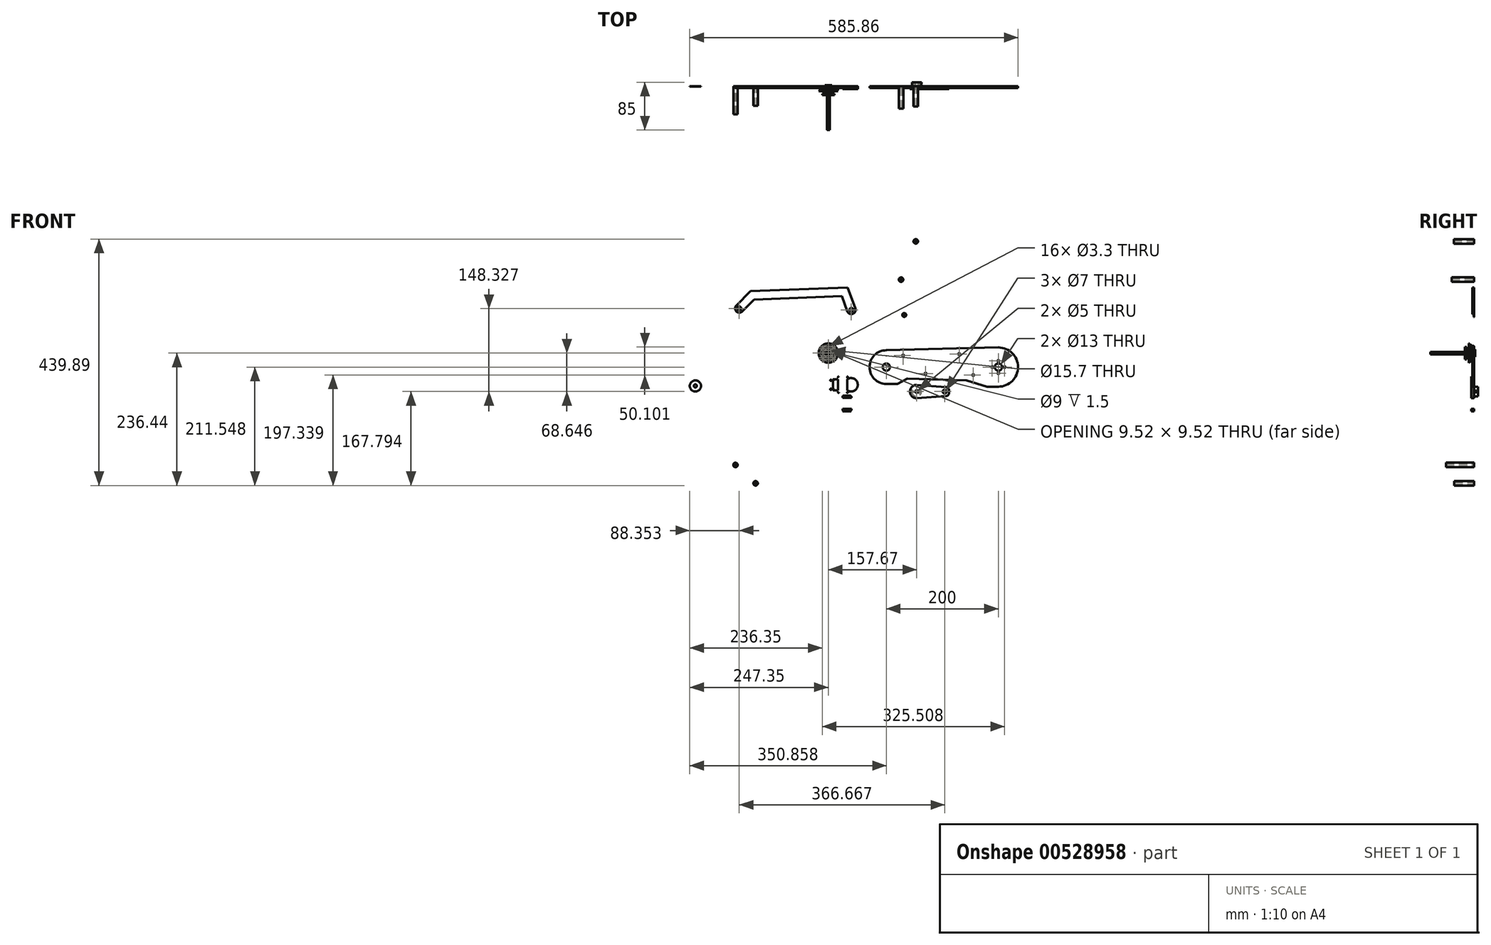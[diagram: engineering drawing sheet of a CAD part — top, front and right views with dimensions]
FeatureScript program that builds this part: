
annotation { "Feature Type Name" : "Feature", "Feature Type Description" : "" }
export const myFeature = defineFeature(function(context is Context, id is Id, definition is map)
    precondition{}
    {
        {
            var Q0;
            Q0=qCreatedBy(makeId("Front.planeOp"),FACE);
            var sketch = newSketch(context, id + "F0", { "sketchPlane" : qUnion([Q0])});
            skCircle(sketch, "E0", {"center": v(103.5, -24.9) * mm, "radius": 6.5 * mm});
            skCircle(sketch, "E1", {"center": v(303.5, -24.9) * mm, "radius": 11 * mm, "construction": true});
            skArc(sketch, "E2", {"start": v(103.5, -54.9) * mm, "mid": v(73.5, -24.9) * mm, "end": v(103.5, 5.1) * mm});
            skLineSegment(sketch, "E3", {"start": v(103.5, -54.9) * mm, "end": v(123.5, -54.9) * mm});
            skArc(sketch, "E4", {"start": v(303.5, -59.9) * mm, "mid": v(338.5, -24.9) * mm, "end": v(303.5, 10.1) * mm});
            skLineSegment(sketch, "E5", {"start": v(303.5, -59.9) * mm, "end": v(283.5, -59.9) * mm});
            skLineSegment(sketch, "E6", {"start": v(103.5, 5.1) * mm, "end": v(303.5, 10.1) * mm});
            skLineSegment(sketch, "E7", {"start": v(123.5, -54.9) * mm, "end": v(283.5, -59.9) * mm, "construction": true});
            skLineSegment(sketch, "E8", {"start": v(123.5, -54.9) * mm, "end": v(141.13, -45.44) * mm});
            skPoint(sketch, "E9", {"position": v(133.5, -4.14) * mm});
            skPoint(sketch, "E10", {"position": v(233.5, -1.64) * mm});
            skLineSegment(sketch, "E11", {"start": v(133.5, -4.14) * mm, "end": v(233.5, -1.64) * mm, "construction": true});
            skPoint(sketch, "E12", {"position": v(173.5, -36.44) * mm});
            skPoint(sketch, "E13", {"position": v(258.5, -39.1) * mm});
            skLineSegment(sketch, "E14", {"start": v(246.52, -48.73) * mm, "end": v(283.5, -59.9) * mm});
            skLineSegment(sketch, "E15", {"start": v(141.13, -45.44) * mm, "end": v(246.52, -48.73) * mm});
            skLineSegment(sketch, "E16", {"start": v(173.5, -36.44) * mm, "end": v(258.5, -39.1) * mm, "construction": true});
            skCircle(sketch, "E17", {"center": v(103.5, 25.51) * mm, "radius": 3.5 * mm});
            skArc(sketch, "E18", {"start": v(98.2, 30.82) * mm, "mid": v(98.2, 20.2) * mm, "end": v(108.81, 20.2) * mm});
            skLineSegment(sketch, "E19", {"start": v(123.68, 56.29) * mm, "end": v(98.2, 30.82) * mm});
            skLineSegment(sketch, "E20", {"start": v(108.81, 20.2) * mm, "end": v(130.12, 41.52) * mm});
            skCircle(sketch, "E21", {"center": v(303.5, 23) * mm, "radius": 3.5 * mm});
            skArc(sketch, "E22", {"start": v(310.56, 25.56) * mm, "mid": v(306.07, 15.95) * mm, "end": v(296.46, 20.43) * mm});
            skLineSegment(sketch, "E23", {"start": v(310.56, 25.56) * mm, "end": v(297, 62.78) * mm});
            skLineSegment(sketch, "E24", {"start": v(296.46, 20.43) * mm, "end": v(286.65, 47.38) * mm});
            skLineSegment(sketch, "E25", {"start": v(123.68, 56.29) * mm, "end": v(297, 62.78) * mm});
            skLineSegment(sketch, "E26", {"start": v(130.12, 41.52) * mm, "end": v(286.65, 47.38) * mm});
            skCircle(sketch, "E27", {"center": v(133.5, -4.14) * mm, "radius": 1.65 * mm});
            skCircle(sketch, "E28", {"center": v(233.5, -1.64) * mm, "radius": 1.65 * mm});
            skCircle(sketch, "E29", {"center": v(173.5, -36.44) * mm, "radius": 1.65 * mm});
            skCircle(sketch, "E30", {"center": v(258.5, -39.1) * mm, "radius": 1.65 * mm});
            skCircle(sketch, "E31", {"center": v(303.5, -24.9) * mm, "radius": 6.5 * mm});
            skPoint(sketch, "E32", {"position": v(314.5, -24.9) * mm});
            skPoint(sketch, "E33", {"position": v(292.5, -24.9) * mm});
            skPoint(sketch, "E34", {"position": v(303.5, -13.9) * mm});
            skPoint(sketch, "E35", {"position": v(303.5, -35.9) * mm});
            skCircle(sketch, "E36", {"center": v(303.5, -13.9) * mm, "radius": 1.65 * mm});
            skCircle(sketch, "E37", {"center": v(314.5, -24.9) * mm, "radius": 1.65 * mm});
            skCircle(sketch, "E38", {"center": v(303.5, -35.9) * mm, "radius": 1.65 * mm});
            skCircle(sketch, "E39", {"center": v(292.5, -24.9) * mm, "radius": 1.65 * mm});
            skSolve(sketch);
        }
        {
            var Q0;
            Q0=makeQuery(id+"F0.imprint","IMPRINT",FACE,{"disambiguationData":[TD([[makeQuery(id+"F0.imprint","IMPRINT",EDGE,{"derivedFrom":sQuery(id+"F0.wireOp",EDGE,"E0")}),-1.0]])]});
            extrude(context, id + "F1", {"entities" : qUnion([Q0]), "depth" : 3 * mm, "offsetDistance" : 25 * mm});
        }
        {
            var Q0;
            Q0=qCreatedBy(makeId("Front.planeOp"),FACE);
            var sketch = newSketch(context, id + "F2", { "sketchPlane" : qUnion([Q0])});
            skCircle(sketch, "E40", {"center": v(-159, 79.68) * mm, "radius": 3.5 * mm});
            skArc(sketch, "E41", {"start": v(-164.3, 84.99) * mm, "mid": v(-164.3, 74.38) * mm, "end": v(-153.7, 74.38) * mm});
            skLineSegment(sketch, "E42", {"start": v(-138.83, 110.46) * mm, "end": v(-164.3, 84.99) * mm});
            skLineSegment(sketch, "E43", {"start": v(-153.7, 74.38) * mm, "end": v(-132.38, 95.69) * mm});
            skCircle(sketch, "E44", {"center": v(41, 77.16) * mm, "radius": 3.5 * mm});
            skArc(sketch, "E45", {"start": v(48.05, 79.73) * mm, "mid": v(43.57, 70.11) * mm, "end": v(33.96, 74.6) * mm});
            skLineSegment(sketch, "E46", {"start": v(48.05, 79.73) * mm, "end": v(34.5, 116.95) * mm});
            skLineSegment(sketch, "E47", {"start": v(33.96, 74.6) * mm, "end": v(24.15, 101.55) * mm});
            skLineSegment(sketch, "E48", {"start": v(-138.83, 110.46) * mm, "end": v(34.5, 116.95) * mm});
            skLineSegment(sketch, "E49", {"start": v(-132.38, 95.69) * mm, "end": v(24.15, 101.55) * mm});
            skSolve(sketch);
        }
        {
            var Q0;
            Q0=makeQuery(id+"F2.imprint","IMPRINT",FACE,{"disambiguationData":[TD([[makeQuery(id+"F2.imprint","IMPRINT",EDGE,{"derivedFrom":sQuery(id+"F2.wireOp",EDGE,"E40")}),-1.0]])]});
            extrude(context, id + "F3", {"entities" : qUnion([Q0]), "depth" : 3 * mm, "offsetDistance" : 25 * mm});
        }
        {
            var Q0;
            Q0=qCreatedBy(makeId("Front.planeOp"),FACE);
            var sketch = newSketch(context, id + "F4", { "sketchPlane" : qUnion([Q0])});
            skLineSegment(sketch, "E50", {"start": v(215.17, -61.15) * mm, "end": v(215.17, -76.15) * mm});
            skCircle(sketch, "E51", {"center": v(207.67, -68.65) * mm, "radius": 3.5 * mm});
            skCircle(sketch, "E52", {"center": v(157.67, -68.65) * mm, "radius": 2.5 * mm});
            skCircle(sketch, "E53", {"center": v(157.67, -68.65) * mm, "radius": 8.5 * mm});
            skArc(sketch, "E54", {"start": v(157.67, -80.65) * mm, "mid": v(145.67, -68.65) * mm, "end": v(157.67, -56.65) * mm});
            skLineSegment(sketch, "E55", {"start": v(157.67, -56.65) * mm, "end": v(215.17, -61.15) * mm});
            skLineSegment(sketch, "E56", {"start": v(215.17, -76.15) * mm, "end": v(157.67, -80.65) * mm});
            skLineSegment(sketch, "E57", {"start": v(157.67, -68.65) * mm, "end": v(215.17, -68.65) * mm, "construction": true});
            skLineSegment(sketch, "E58.bottom", {"start": v(160.57, -71.45) * mm, "end": v(163.27, -71.45) * mm});
            skLineSegment(sketch, "E58.top", {"start": v(160.57, -65.85) * mm, "end": v(163.27, -65.85) * mm});
            skLineSegment(sketch, "E58.left", {"start": v(160.57, -71.45) * mm, "end": v(160.57, -65.85) * mm});
            skLineSegment(sketch, "E58.right", {"start": v(163.27, -71.45) * mm, "end": v(163.27, -65.85) * mm});
            skSolve(sketch);
        }
        {
            var Q0;
            Q0=makeQuery(id+"F4.imprint","IMPRINT",FACE,{"disambiguationData":[TD([[makeQuery(id+"F4.imprint","IMPRINT",EDGE,{"derivedFrom":sQuery(id+"F4.wireOp",EDGE,"E52")}),-1.0]])]});
            var Q1;
            Q1=makeQuery(id+"F4.imprint","IMPRINT",FACE,{"disambiguationData":[TD([[makeQuery(id+"F4.imprint","IMPRINT",EDGE,{"derivedFrom":sQuery(id+"F4.wireOp",EDGE,"E50")}),-1.0]])]});
            var Q2;
            Q2=makeQuery(id+"F4.imprint","IMPRINT",FACE,{"disambiguationData":[TD([[makeQuery(id+"F4.imprint","IMPRINT",EDGE,{"derivedFrom":sQuery(id+"F4.wireOp",EDGE,"E58.bottom")}),1.0]])]});
            extrude(context, id + "F5", {"entities" : qUnion([Q0, Q1, Q2]), "depth" : 5 * mm, "offsetDistance" : 25 * mm});
        }
        {
            var Q0;
            Q0=makeQuery(id+"F4.imprint","IMPRINT",FACE,{"disambiguationData":[TD([[makeQuery(id+"F4.imprint","IMPRINT",EDGE,{"derivedFrom":sQuery(id+"F4.wireOp",EDGE,"E52")}),-1.0]])]});
            extrude(context, id + "F6", {"entities" : qUnion([Q0]), "operationType" : NewBodyOperationType.ADD, "oppositeDirection" : true, "depth" : 7 * mm, "offsetDistance" : 25 * mm});
        }
        {
            var Q0;
            Q0=makeQuery(id+"F5.opExtrude","SWEPT_EDGE",EDGE,{"disambiguationData":[OSD([sQuery(id+"F4.wireOp",EDGE,"E50"),sQuery(id+"F4.wireOp",EDGE,"E55")])]});
            var Q1;
            Q1=makeQuery(id+"F5.opExtrude","SWEPT_EDGE",EDGE,{"disambiguationData":[OSD([sQuery(id+"F4.wireOp",EDGE,"E50"),sQuery(id+"F4.wireOp",EDGE,"E56")])]});
            fillet(context, id + "F7", {"entities" : qUnion([Q0, Q1]), "radius" : 5 * mm, "tangentPropagation" : true, "allowEdgeOverflow" : false});
        }
        {
            var Q0;
            Q0=makeQuery(id+"F6.opExtrude","SWEPT_FACE",FACE,{"disambiguationData":[OSD([sQuery(id+"F4.wireOp",EDGE,"E58.left")])]});
            var sketch = newSketch(context, id + "F8", { "sketchPlane" : qUnion([Q0])});
            skLineSegment(sketch, "E59", {"start": v(3.5, -71.45) * mm, "end": v(3.5, -65.85) * mm, "construction": true});
            skPoint(sketch, "E60", {"position": v(3.5, -68.65) * mm});
            skSolve(sketch);
        }
        {
            var Q0;
            Q0=sQuery(id+"F8.wireOp",VERTEX,"E60");
            var Q1;
            Q1=makeQuery(id+"F5.opExtrude","SWEPT_BODY",BODY,{"disambiguationData":[OSD([sQuery(id+"F4.wireOp",EDGE,"E50"),sQuery(id+"F4.wireOp",EDGE,"E51"),sQuery(id+"F4.wireOp",EDGE,"E52"),sQuery(id+"F4.wireOp",EDGE,"E54"),sQuery(id+"F4.wireOp",EDGE,"E55"),sQuery(id+"F4.wireOp",EDGE,"E56")])]});
            hole(context, id + "F9", {"style" : HoleStyle.SIMPLE, "endStyle" : HoleEndStyle.THROUGH, "oppositeDirection" : true, "standardTappedOrClearance" : lookupTablePath({ "standard" : "ISO", "engagement" : "75%", "pitch" : "0.5 mm", "size" : "M3", "type" : "Tapped" }), "standardBlindInLast" : lookupTablePath({ "standard" : "ISO", "engagement" : "75%", "pitch" : "0.5 mm", "size" : "M3", "type" : "Tapped" }), "holeDiameter" : 2.5 * mm, "majorDiameter" : 3 * mm, "showTappedDepth" : true, "isTappedThrough" : true, "tappedDepth" : 12 * mm, "tapClearance" : 3, "locations" : qUnion([Q0]), "scope" : qUnion([Q1])});
        }
        {
            var Q0;
            Q0=sQuery(id+"F8.wireOp",VERTEX,"E60");
            var Q1;
            Q1=makeQuery(id+"F5.opExtrude","SWEPT_BODY",BODY,{"disambiguationData":[OSD([sQuery(id+"F4.wireOp",EDGE,"E50"),sQuery(id+"F4.wireOp",EDGE,"E51"),sQuery(id+"F4.wireOp",EDGE,"E52"),sQuery(id+"F4.wireOp",EDGE,"E54"),sQuery(id+"F4.wireOp",EDGE,"E55"),sQuery(id+"F4.wireOp",EDGE,"E56")])]});
            hole(context, id + "F10", {"style" : HoleStyle.SIMPLE, "endStyle" : HoleEndStyle.THROUGH, "standardTappedOrClearance" : lookupTablePath({ "standard" : "ISO", "engagement" : "75%", "pitch" : "0.5 mm", "size" : "M3", "type" : "Tapped" }), "standardBlindInLast" : lookupTablePath({ "standard" : "ISO", "engagement" : "75%", "pitch" : "0.5 mm", "size" : "M3", "type" : "Tapped" }), "holeDiameter" : 2.5 * mm, "majorDiameter" : 3 * mm, "showTappedDepth" : true, "isTappedThrough" : true, "tappedDepth" : 12 * mm, "tapClearance" : 3, "locations" : qUnion([Q0]), "scope" : qUnion([Q1])});
        }
        {
            var Q0;
            Q0=qCreatedBy(makeId("Front.planeOp"),FACE);
            var sketch = newSketch(context, id + "F11", { "sketchPlane" : qUnion([Q0])});
            skCircle(sketch, "E61", {"center": v(0, 0) * mm, "radius": 15.03 * mm});
            skCircle(sketch, "E62", {"center": v(-7.97, 12.74) * mm, "radius": 0.85 * mm});
            skArc(sketch, "E63", {"start": v(-8.6, 12.33) * mm, "mid": v(-7.58, 12.1) * mm, "end": v(-7.33, 13.13) * mm, "construction": true});
            skSolve(sketch);
        }
        {
            var Q0;
            {var subQ0=sQuery(id+"F11.wireOp",EDGE,"E62");var subQ1=sQuery(id+"F11.wireOp",EDGE,"E61");var subQ2=makeQuery(id+"F11.imprint","INTERSECT",VERTEX,{"disambiguationData":[OD(0.0)],"derivedFrom":[subQ1,subQ0]});Q0=makeQuery(id+"F11.imprint","IMPRINT",FACE,{"disambiguationData":[TD([[makeQuery(id+"F11.imprint","IMPRINT",EDGE,{"disambiguationData":[TD([[subQ2,-1.0]])],"derivedFrom":subQ1}),1.0]])]});}
            extrude(context, id + "F12", {"entities" : qUnion([Q0]), "depth" : 7 * mm, "offsetDistance" : 25 * mm});
        }
        {
            var Q0;
            {var subQ0=sQuery(id+"F11.wireOp",EDGE,"E62");var subQ1=sQuery(id+"F11.wireOp",EDGE,"E61");Q0=makeQuery(id+"F12.opExtrude","SWEPT_EDGE",EDGE,{"disambiguationData":[OSD([subQ1,subQ0]),TDD([makeQuery(id+"F11.imprint","INTERSECT",VERTEX,{"disambiguationData":[OD(0.0)],"derivedFrom":[subQ1,subQ0]})])]});}
            var Q1;
            {var subQ0=sQuery(id+"F11.wireOp",EDGE,"E62");var subQ1=sQuery(id+"F11.wireOp",EDGE,"E61");Q1=makeQuery(id+"F12.opExtrude","SWEPT_EDGE",EDGE,{"disambiguationData":[OSD([subQ1,subQ0]),TDD([makeQuery(id+"F11.imprint","INTERSECT",VERTEX,{"disambiguationData":[OD(1.0)],"derivedFrom":[subQ1,subQ0]})])]});}
            fillet(context, id + "F13", {"entities" : qUnion([Q0, Q1]), "radius" : 0.05 * mm, "tangentPropagation" : true, "allowEdgeOverflow" : false});
        }
        {
            var Q0;
            Q0=makeQuery(id+"F12.opExtrude","SWEPT_FACE",FACE,{"disambiguationData":[OSD([sQuery(id+"F11.wireOp",EDGE,"E62")])]});
            var Q1;
            {var subQ0=sQuery(id+"F11.wireOp",EDGE,"E62");var subQ1=sQuery(id+"F11.wireOp",EDGE,"E61");Q1=makeQuery(id+"F13.opFillet","BLEND_FACE",FACE,{"disambiguationData":[OSD([subQ1,subQ0]),TDD([makeQuery(id+"F12.opExtrude","SWEPT_EDGE",EDGE,{"disambiguationData":[OSD([subQ1,subQ0]),TDD([makeQuery(id+"F11.imprint","INTERSECT",VERTEX,{"disambiguationData":[OD(0.0)],"derivedFrom":[subQ1,subQ0]})])]})])]});}
            var Q2;
            {var subQ0=sQuery(id+"F11.wireOp",EDGE,"E62");var subQ1=sQuery(id+"F11.wireOp",EDGE,"E61");Q2=makeQuery(id+"F13.opFillet","BLEND_FACE",FACE,{"disambiguationData":[OSD([subQ1,subQ0]),TDD([makeQuery(id+"F12.opExtrude","SWEPT_EDGE",EDGE,{"disambiguationData":[OSD([subQ1,subQ0]),TDD([makeQuery(id+"F11.imprint","INTERSECT",VERTEX,{"disambiguationData":[OD(1.0)],"derivedFrom":[subQ1,subQ0]})])]})])]});}
            var Q3;
            Q3=makeQuery(id+"F12.opExtrude","SWEPT_FACE",FACE,{"disambiguationData":[OSD([sQuery(id+"F11.wireOp",EDGE,"E61")])]});
            circularPattern(context, id + "F14", {"patternType" : PatternType.FACE, "faces" : qUnion([Q0, Q1, Q2]), "axis" : qUnion([Q3]), "angle" : 360 * degree, "instanceCount" : 48, "equalSpace" : true});
        }
        {
            var Q0;
            Q0=qCreatedBy(makeId("Right.planeOp"),FACE);
            var sketch = newSketch(context, id + "F15", { "sketchPlane" : qUnion([Q0])});
            skLineSegment(sketch, "E64", {"start": v(0, 0) * mm, "end": v(0, 15.2) * mm});
            skLineSegment(sketch, "E65", {"start": v(0, 15.2) * mm, "end": v(2, 17.2) * mm});
            skLineSegment(sketch, "E66", {"start": v(2, 17.2) * mm, "end": v(2, 0) * mm});
            skLineSegment(sketch, "E67", {"start": v(2, 0) * mm, "end": v(0, 0) * mm});
            skLineSegment(sketch, "E68.MirrorCS", {"start": v(-9, 17.25) * mm, "end": v(-9, 0) * mm});
            skLineSegment(sketch, "E69.MirrorCS", {"start": v(-7, 15.25) * mm, "end": v(-9, 17.25) * mm});
            skLineSegment(sketch, "E70.MirrorCS", {"start": v(-7, 0) * mm, "end": v(-7, 15.25) * mm});
            skLineSegment(sketch, "E71.MirrorCS", {"start": v(-9, 0) * mm, "end": v(-7, 0) * mm});
            skSolve(sketch);
        }
        {
            var Q0;
            Q0=makeQuery(id+"F15.imprint","IMPRINT",FACE,{"disambiguationData":[TD([[makeQuery(id+"F15.imprint","IMPRINT",EDGE,{"derivedFrom":sQuery(id+"F15.wireOp",EDGE,"E64")}),-1.0]])]});
            var Q1;
            Q1=makeQuery(id+"F15.imprint","IMPRINT",FACE,{"disambiguationData":[TD([[makeQuery(id+"F15.imprint","IMPRINT",EDGE,{"derivedFrom":sQuery(id+"F15.wireOp",EDGE,"E68.MirrorCS")}),1.0]])]});
            var Q2;
            Q2=sQuery(id+"F15.wireOp",EDGE,"E67");
            revolve(context, id + "F16", {"operationType" : NewBodyOperationType.ADD, "entities" : qUnion([Q0, Q1]), "axis" : qUnion([Q2]), "revolveType" : RevolveType.FULL});
        }
        {
            var Q0;
            Q0=makeQuery(id+"F16.opRevolve","SWEPT_FACE",FACE,{"disambiguationData":[OSD([sQuery(id+"F15.wireOp",EDGE,"E66")])]});
            var sketch = newSketch(context, id + "F17", { "sketchPlane" : qUnion([Q0])});
            skCircle(sketch, "E72", {"center": v(0, 0) * mm, "radius": 11 * mm, "construction": true});
            skCircle(sketch, "E73", {"center": v(0, 0) * mm, "radius": 7.85 * mm});
            skCircle(sketch, "E74", {"center": v(0, 11) * mm, "radius": 1.65 * mm});
            skCircle(sketch, "E75", {"center": v(11, 0) * mm, "radius": 1.65 * mm});
            skCircle(sketch, "E76", {"center": v(0, -11) * mm, "radius": 1.65 * mm});
            skCircle(sketch, "E77", {"center": v(-11, 0) * mm, "radius": 1.65 * mm});
            skSolve(sketch);
        }
        {
            var Q0;
            Q0 = qSketchRegion(id + "F17", true);
            extrude(context, id + "F18", {"entities" : qUnion([Q0]), "operationType" : NewBodyOperationType.REMOVE, "oppositeDirection" : true, "depth" : 25 * mm, "offsetDistance" : 25 * mm});
        }
        {
            var Q0;
            Q0=qCreatedBy(makeId("Front.planeOp"),FACE);
            var sketch = newSketch(context, id + "F19", { "sketchPlane" : qUnion([Q0])});
            skCircle(sketch, "E78", {"center": v(0, 0) * mm, "radius": 4.84 * mm});
            skCircle(sketch, "E79", {"center": v(0, 4.84) * mm, "radius": 0.75 * mm, "construction": true});
            skCircle(sketch, "E80", {"center": v(0, 4.84) * mm, "radius": 0.85 * mm});
            skSolve(sketch);
        }
        {
            var Q0;
            {var subQ0=sQuery(id+"F19.wireOp",EDGE,"E80");var subQ1=sQuery(id+"F19.wireOp",EDGE,"E78");var subQ2=makeQuery(id+"F19.imprint","INTERSECT",VERTEX,{"disambiguationData":[OD(0.0)],"derivedFrom":[subQ1,subQ0]});Q0=makeQuery(id+"F19.imprint","IMPRINT",FACE,{"disambiguationData":[TD([[makeQuery(id+"F19.imprint","IMPRINT",EDGE,{"disambiguationData":[TD([[subQ2,-1.0]])],"derivedFrom":subQ1}),1.0]])]});}
            extrude(context, id + "F20", {"entities" : qUnion([Q0]), "depth" : 7 * mm, "offsetDistance" : 25 * mm});
        }
        {
            var Q0;
            {var subQ0=sQuery(id+"F19.wireOp",EDGE,"E80");var subQ1=sQuery(id+"F19.wireOp",EDGE,"E78");Q0=makeQuery(id+"F20.opExtrude","SWEPT_EDGE",EDGE,{"disambiguationData":[OSD([subQ1,subQ0]),TDD([makeQuery(id+"F19.imprint","INTERSECT",VERTEX,{"disambiguationData":[OD(0.0)],"derivedFrom":[subQ1,subQ0]})])]});}
            var Q1;
            {var subQ0=sQuery(id+"F19.wireOp",EDGE,"E80");var subQ1=sQuery(id+"F19.wireOp",EDGE,"E78");Q1=makeQuery(id+"F20.opExtrude","SWEPT_EDGE",EDGE,{"disambiguationData":[OSD([subQ1,subQ0]),TDD([makeQuery(id+"F19.imprint","INTERSECT",VERTEX,{"disambiguationData":[OD(1.0)],"derivedFrom":[subQ1,subQ0]})])]});}
            fillet(context, id + "F21", {"entities" : qUnion([Q0, Q1]), "radius" : 0.05 * mm, "tangentPropagation" : true, "allowEdgeOverflow" : false});
        }
        {
            var Q0;
            Q0=makeQuery(id+"F20.opExtrude","SWEPT_FACE",FACE,{"disambiguationData":[OSD([sQuery(id+"F19.wireOp",EDGE,"E80")])]});
            var Q1;
            {var subQ0=sQuery(id+"F19.wireOp",EDGE,"E80");var subQ1=sQuery(id+"F19.wireOp",EDGE,"E78");Q1=makeQuery(id+"F21.opFillet","BLEND_FACE",FACE,{"disambiguationData":[OSD([subQ1,subQ0]),TDD([makeQuery(id+"F20.opExtrude","SWEPT_EDGE",EDGE,{"disambiguationData":[OSD([subQ1,subQ0]),TDD([makeQuery(id+"F19.imprint","INTERSECT",VERTEX,{"disambiguationData":[OD(0.0)],"derivedFrom":[subQ1,subQ0]})])]})])]});}
            var Q2;
            {var subQ0=sQuery(id+"F19.wireOp",EDGE,"E80");var subQ1=sQuery(id+"F19.wireOp",EDGE,"E78");Q2=makeQuery(id+"F21.opFillet","BLEND_FACE",FACE,{"disambiguationData":[OSD([subQ1,subQ0]),TDD([makeQuery(id+"F20.opExtrude","SWEPT_EDGE",EDGE,{"disambiguationData":[OSD([subQ1,subQ0]),TDD([makeQuery(id+"F19.imprint","INTERSECT",VERTEX,{"disambiguationData":[OD(1.0)],"derivedFrom":[subQ1,subQ0]})])]})])]});}
            var Q3;
            Q3=makeQuery(id+"F20.opExtrude","SWEPT_FACE",FACE,{"disambiguationData":[OSD([sQuery(id+"F19.wireOp",EDGE,"E78")])]});
            circularPattern(context, id + "F22", {"patternType" : PatternType.FACE, "faces" : qUnion([Q0, Q1, Q2]), "axis" : qUnion([Q3]), "angle" : 360 * degree, "instanceCount" : 16, "equalSpace" : true});
        }
        {
            var Q0;
            Q0=qCreatedBy(makeId("Right.planeOp"),FACE);
            var sketch = newSketch(context, id + "F23", { "sketchPlane" : qUnion([Q0])});
            skLineSegment(sketch, "E81", {"start": v(0, 0) * mm, "end": v(0, 5) * mm});
            skLineSegment(sketch, "E82", {"start": v(0, 5) * mm, "end": v(2, 7) * mm});
            skLineSegment(sketch, "E83", {"start": v(2, 7) * mm, "end": v(2, 0) * mm});
            skLineSegment(sketch, "E84", {"start": v(2, 0) * mm, "end": v(0, 0) * mm});
            skLineSegment(sketch, "E85", {"start": v(-7, 5) * mm, "end": v(-7, 0) * mm});
            skLineSegment(sketch, "E86", {"start": v(-7, 5) * mm, "end": v(-9, 7) * mm});
            skLineSegment(sketch, "E87", {"start": v(-9, 7) * mm, "end": v(-13, 7) * mm});
            skLineSegment(sketch, "E88", {"start": v(-13, 7) * mm, "end": v(-13, 11) * mm});
            skLineSegment(sketch, "E89", {"start": v(-13, 11) * mm, "end": v(-16, 11) * mm});
            skLineSegment(sketch, "E90", {"start": v(-16, 11) * mm, "end": v(-16, 4.5) * mm});
            skLineSegment(sketch, "E91", {"start": v(-16, 4.5) * mm, "end": v(-14.5, 4.5) * mm});
            skLineSegment(sketch, "E92", {"start": v(-14.5, 4.5) * mm, "end": v(-14.5, 0) * mm});
            skLineSegment(sketch, "E93", {"start": v(-14.5, 0) * mm, "end": v(-7, 0) * mm});
            skSolve(sketch);
        }
        {
            var Q0;
            Q0=makeQuery(id+"F23.imprint","IMPRINT",FACE,{"disambiguationData":[TD([[makeQuery(id+"F23.imprint","IMPRINT",EDGE,{"derivedFrom":sQuery(id+"F23.wireOp",EDGE,"E85")}),-1.0]])]});
            var Q1;
            Q1=makeQuery(id+"F23.imprint","IMPRINT",FACE,{"disambiguationData":[TD([[makeQuery(id+"F23.imprint","IMPRINT",EDGE,{"derivedFrom":sQuery(id+"F23.wireOp",EDGE,"E81")}),-1.0]])]});
            var Q2;
            Q2=sQuery(id+"F23.wireOp",EDGE,"E93");
            revolve(context, id + "F24", {"operationType" : NewBodyOperationType.ADD, "entities" : qUnion([Q0, Q1]), "axis" : qUnion([Q2]), "revolveType" : RevolveType.FULL});
        }
        {
            var Q0;
            Q0=makeQuery(id+"F24.opRevolve","SWEPT_FACE",FACE,{"disambiguationData":[OSD([sQuery(id+"F23.wireOp",EDGE,"E85")])]});
            var sketch = newSketch(context, id + "F25", { "sketchPlane" : qUnion([Q0])});
            skCircle(sketch, "E94", {"center": v(0, 0) * mm, "radius": 8 * mm, "construction": true});
            skPoint(sketch, "E95", {"position": v(0, 8) * mm});
            skPoint(sketch, "E96", {"position": v(-8, 0) * mm});
            skPoint(sketch, "E97", {"position": v(0, -8) * mm});
            skPoint(sketch, "E98", {"position": v(8, 0) * mm});
            skSolve(sketch);
        }
        {
            var Q0;
            Q0=sQuery(id+"F25.wireOp",VERTEX,"E95");
            var Q1;
            Q1=sQuery(id+"F25.wireOp",VERTEX,"E98");
            var Q2;
            Q2=sQuery(id+"F25.wireOp",VERTEX,"E96");
            var Q3;
            Q3=sQuery(id+"F25.wireOp",VERTEX,"E97");
            var Q4;
            Q4=makeQuery(id+"F20.opExtrude","SWEPT_BODY",BODY,{"disambiguationData":[OSD([sQuery(id+"F19.wireOp",EDGE,"E78"),sQuery(id+"F19.wireOp",EDGE,"E80")])]});
            hole(context, id + "F26", {"style" : HoleStyle.SIMPLE, "endStyle" : HoleEndStyle.THROUGH, "holeDiameter" : 3.3 * mm, "majorDiameter" : 5 * mm, "isTappedThrough" : true, "tappedDepth" : 12 * mm, "tapClearance" : 3, "locations" : qUnion([Q0, Q1, Q2, Q3]), "scope" : qUnion([Q4])});
        }
        {
            var Q0;
            Q0=qCreatedBy(makeId("Front.planeOp"),FACE);
            var sketch = newSketch(context, id + "F27", { "sketchPlane" : qUnion([Q0])});
            skArc(sketch, "E99", {"start": v(27.19, 12.68) * mm, "mid": v(-12.68, 27.19) * mm, "end": v(-27.19, -12.68) * mm});
            skCircle(sketch, "E100", {"center": v(0, 0) * mm, "radius": 6.5 * mm});
            skLineSegment(sketch, "E101", {"start": v(-27.19, -12.68) * mm, "end": v(-0.46, -70) * mm});
            skLineSegment(sketch, "E102", {"start": v(27.19, 12.68) * mm, "end": v(59.54, -56.7) * mm});
            skLineSegment(sketch, "E103", {"start": v(-0.46, -70) * mm, "end": v(-0.46, -150) * mm});
            skLineSegment(sketch, "E104", {"start": v(-0.46, -150) * mm, "end": v(59.54, -150) * mm, "construction": true});
            skLineSegment(sketch, "E105", {"start": v(59.54, -56.7) * mm, "end": v(59.54, -150) * mm});
            skLineSegment(sketch, "E106", {"start": v(-0.46, -150) * mm, "end": v(-0.46, -155) * mm});
            skLineSegment(sketch, "E107", {"start": v(-0.46, -155) * mm, "end": v(19.54, -155) * mm});
            skLineSegment(sketch, "E108", {"start": v(19.54, -155) * mm, "end": v(19.54, -150) * mm});
            skLineSegment(sketch, "E109", {"start": v(19.54, -150) * mm, "end": v(39.54, -150) * mm});
            skLineSegment(sketch, "E110", {"start": v(39.54, -150) * mm, "end": v(39.54, -155) * mm});
            skLineSegment(sketch, "E111", {"start": v(39.54, -155) * mm, "end": v(59.54, -155) * mm});
            skLineSegment(sketch, "E112", {"start": v(59.54, -155) * mm, "end": v(59.54, -150) * mm});
            skSolve(sketch);
        }
        {
            var Q0;
            Q0=makeQuery(id+"F27.imprint","IMPRINT",FACE,{"disambiguationData":[TD([[makeQuery(id+"F27.imprint","IMPRINT",EDGE,{"derivedFrom":sQuery(id+"F27.wireOp",EDGE,"E99")}),1.0]])]});
            extrude(context, id + "F28", {"entities" : qUnion([Q0]), "depth" : 5 * mm, "offsetDistance" : 25 * mm});
        }
        {
            var Q0;
            Q0=makeQuery(id+"F28.opExtrude","SWEPT_BODY",BODY,{"disambiguationData":[OSD([sQuery(id+"F27.wireOp",EDGE,"E99"),sQuery(id+"F27.wireOp",EDGE,"E100"),sQuery(id+"F27.wireOp",EDGE,"E101"),sQuery(id+"F27.wireOp",EDGE,"E102"),sQuery(id+"F27.wireOp",EDGE,"E103"),sQuery(id+"F27.wireOp",EDGE,"E105"),sQuery(id+"F27.wireOp",EDGE,"E106"),sQuery(id+"F27.wireOp",EDGE,"E107"),sQuery(id+"F27.wireOp",EDGE,"E108"),sQuery(id+"F27.wireOp",EDGE,"E109"),sQuery(id+"F27.wireOp",EDGE,"E110"),sQuery(id+"F27.wireOp",EDGE,"E111"),sQuery(id+"F27.wireOp",EDGE,"E112")])]});
            transform(context, id + "F29", {"entities" : qUnion([Q0]), "transformType" : TransformType.COPY});
        }
        {
            var Q0;
            Q0=makeQuery(id+"F27.imprint","IMPRINT",FACE,{"disambiguationData":[TD([[makeQuery(id+"F27.imprint","IMPRINT",EDGE,{"derivedFrom":sQuery(id+"F27.wireOp",EDGE,"E99")}),1.0]])]});
            var sketch = newSketch(context, id + "F30", { "sketchPlane" : qUnion([Q0])});
            skLineSegment(sketch, "E113.bottom", {"start": v(17.54, -42) * mm, "end": v(33.54, -42) * mm});
            skLineSegment(sketch, "E113.top", {"start": v(17.54, -70) * mm, "end": v(33.54, -70) * mm});
            skLineSegment(sketch, "E113.left", {"start": v(17.54, -42) * mm, "end": v(17.54, -70) * mm});
            skLineSegment(sketch, "E113.right", {"start": v(33.54, -42) * mm, "end": v(33.54, -70) * mm});
            skCircle(sketch, "E114", {"center": v(18.54, -89.5) * mm, "radius": 12 * mm});
            skLineSegment(sketch, "E115", {"start": v(25.17, -99.5) * mm, "end": v(51.04, -99.5) * mm});
            skLineSegment(sketch, "E116", {"start": v(51.04, -99.5) * mm, "end": v(51.04, -79.5) * mm});
            skLineSegment(sketch, "E117", {"start": v(51.04, -79.5) * mm, "end": v(25.17, -79.5) * mm});
            skLineSegment(sketch, "E118", {"start": v(51.04, -89.5) * mm, "end": v(18.54, -89.5) * mm, "construction": true});
            skPoint(sketch, "E119", {"position": v(41.04, -103) * mm});
            skPoint(sketch, "E120", {"position": v(41.04, -76) * mm});
            skPoint(sketch, "E121", {"position": v(54.54, -81.5) * mm});
            skPoint(sketch, "E122", {"position": v(54.54, -97.5) * mm});
            skPoint(sketch, "E123", {"position": v(25.04, -103) * mm});
            skPoint(sketch, "E124", {"position": v(25.04, -76) * mm});
            skCircle(sketch, "E125", {"center": v(25.04, -76) * mm, "radius": 1.1 * mm});
            skCircle(sketch, "E126", {"center": v(41.04, -76) * mm, "radius": 1.1 * mm});
            skCircle(sketch, "E127", {"center": v(54.54, -81.5) * mm, "radius": 1.1 * mm});
            skCircle(sketch, "E128", {"center": v(54.54, -97.5) * mm, "radius": 1.1 * mm});
            skCircle(sketch, "E129", {"center": v(41.04, -103) * mm, "radius": 1.1 * mm});
            skCircle(sketch, "E130", {"center": v(25.04, -103) * mm, "radius": 1.1 * mm});
            skLineSegment(sketch, "E131.bottom", {"start": v(41.54, -129) * mm, "end": v(51.54, -129) * mm});
            skLineSegment(sketch, "E131.top", {"start": v(41.54, -144) * mm, "end": v(51.54, -144) * mm});
            skLineSegment(sketch, "E131.left", {"start": v(41.54, -129) * mm, "end": v(41.54, -144) * mm});
            skLineSegment(sketch, "E131.right", {"start": v(51.54, -129) * mm, "end": v(51.54, -144) * mm});
            skCircle(sketch, "E132", {"center": v(8.5, -48.35) * mm, "radius": 1.1 * mm});
            skCircle(sketch, "E133", {"center": v(8.5, -64.35) * mm, "radius": 1.1 * mm});
            skSolve(sketch);
        }
        {
            var Q0;
            Q0 = qSketchRegion(id + "F30", true);
            extrude(context, id + "F31", {"entities" : qUnion([Q0]), "operationType" : NewBodyOperationType.REMOVE, "depth" : 25 * mm, "offsetDistance" : 25 * mm});
        }
        {
            var Q0;
            Q0=makeQuery(id+"F29.opPattern","COPY",FACE,{"derivedFrom":makeQuery(id+"F28.opExtrude","CAP_FACE",FACE,{"disambiguationData":[OSD([sQuery(id+"F27.wireOp",EDGE,"E99"),sQuery(id+"F27.wireOp",EDGE,"E100"),sQuery(id+"F27.wireOp",EDGE,"E101"),sQuery(id+"F27.wireOp",EDGE,"E102"),sQuery(id+"F27.wireOp",EDGE,"E103"),sQuery(id+"F27.wireOp",EDGE,"E105"),sQuery(id+"F27.wireOp",EDGE,"E106"),sQuery(id+"F27.wireOp",EDGE,"E107"),sQuery(id+"F27.wireOp",EDGE,"E108"),sQuery(id+"F27.wireOp",EDGE,"E109"),sQuery(id+"F27.wireOp",EDGE,"E110"),sQuery(id+"F27.wireOp",EDGE,"E111"),sQuery(id+"F27.wireOp",EDGE,"E112")])],"isStart":false}),"instanceName":"1"});
            var sketch = newSketch(context, id + "F32", { "sketchPlane" : qUnion([Q0])});
            skLineSegment(sketch, "E134.bottom", {"start": v(25.54, -76) * mm, "end": v(41.54, -76) * mm});
            skLineSegment(sketch, "E134.top", {"start": v(25.54, -104) * mm, "end": v(41.54, -104) * mm});
            skLineSegment(sketch, "E134.left", {"start": v(25.54, -76) * mm, "end": v(25.54, -104) * mm});
            skLineSegment(sketch, "E134.right", {"start": v(41.54, -76) * mm, "end": v(41.54, -104) * mm});
            skCircle(sketch, "E135.MirrorC", {"center": v(40.54, -56.5) * mm, "radius": 12 * mm});
            skLineSegment(sketch, "E136.MirrorCS", {"start": v(8.04, -46.5) * mm, "end": v(33.9, -46.5) * mm});
            skCircle(sketch, "E137.MirrorC", {"center": v(34.04, -43) * mm, "radius": 1.1 * mm});
            skCircle(sketch, "E138.MirrorC", {"center": v(34.04, -70) * mm, "radius": 1.1 * mm});
            skCircle(sketch, "E139.MirrorC", {"center": v(18.04, -70) * mm, "radius": 1.1 * mm});
            skLineSegment(sketch, "E140.MirrorCS", {"start": v(8.04, -66.5) * mm, "end": v(8.04, -46.5) * mm});
            skLineSegment(sketch, "E141.MirrorCS", {"start": v(33.9, -66.5) * mm, "end": v(8.04, -66.5) * mm});
            skCircle(sketch, "E142.MirrorC", {"center": v(4.54, -48.5) * mm, "radius": 1.1 * mm});
            skCircle(sketch, "E143.MirrorC", {"center": v(4.54, -64.5) * mm, "radius": 1.1 * mm});
            skCircle(sketch, "E144.MirrorC", {"center": v(18.04, -43) * mm, "radius": 1.1 * mm});
            skLineSegment(sketch, "E145", {"start": v(40.54, -56.5) * mm, "end": v(8.04, -56.5) * mm, "construction": true});
            skLineSegment(sketch, "E146.bottom", {"start": v(41.54, -129) * mm, "end": v(51.54, -129) * mm});
            skLineSegment(sketch, "E146.top", {"start": v(41.54, -144) * mm, "end": v(51.54, -144) * mm});
            skLineSegment(sketch, "E146.left", {"start": v(41.54, -129) * mm, "end": v(41.54, -144) * mm});
            skLineSegment(sketch, "E146.right", {"start": v(51.54, -129) * mm, "end": v(51.54, -144) * mm});
            skCircle(sketch, "E147", {"center": v(54.54, -81.5) * mm, "radius": 1.1 * mm});
            skCircle(sketch, "E148", {"center": v(54.54, -97.5) * mm, "radius": 1.1 * mm});
            skSolve(sketch);
        }
        {
            var Q0;
            {var subQ0=sQuery(id+"F32.wireOp",EDGE,"E136.MirrorCS");Q0=makeQuery(id+"F32.imprint","IMPRINT",FACE,{"disambiguationData":[TD([[makeQuery(id+"F32.imprint","IMPRINT",EDGE,{"derivedFrom":subQ0}),-1.0]])]});}
            var Q1;
            {var subQ0=sQuery(id+"F32.wireOp",EDGE,"E135.MirrorC");var subQ1=makeQuery(id+"F32.imprint","INTERSECT",VERTEX,{"derivedFrom":[subQ0,sQuery(id+"F32.wireOp",EDGE,"E136.MirrorCS")]});Q1=makeQuery(id+"F32.imprint","IMPRINT",FACE,{"disambiguationData":[TD([[makeQuery(id+"F32.imprint","IMPRINT",EDGE,{"disambiguationData":[TD([[subQ1,-1.0]])],"derivedFrom":subQ0}),-1.0]])]});}
            var Q2;
            Q2=makeQuery(id+"F32.imprint","IMPRINT",FACE,{"disambiguationData":[TD([[makeQuery(id+"F32.imprint","IMPRINT",EDGE,{"derivedFrom":sQuery(id+"F32.wireOp",EDGE,"E134.bottom")}),-1.0]])]});
            var Q3;
            Q3=makeQuery(id+"F32.imprint","IMPRINT",FACE,{"disambiguationData":[TD([[makeQuery(id+"F32.imprint","IMPRINT",EDGE,{"derivedFrom":sQuery(id+"F32.wireOp",EDGE,"E144.MirrorC")}),-1.0]])]});
            var Q4;
            Q4=makeQuery(id+"F32.imprint","IMPRINT",FACE,{"disambiguationData":[TD([[makeQuery(id+"F32.imprint","IMPRINT",EDGE,{"derivedFrom":sQuery(id+"F32.wireOp",EDGE,"E137.MirrorC")}),-1.0]])]});
            var Q5;
            Q5=makeQuery(id+"F32.imprint","IMPRINT",FACE,{"disambiguationData":[TD([[makeQuery(id+"F32.imprint","IMPRINT",EDGE,{"derivedFrom":sQuery(id+"F32.wireOp",EDGE,"E138.MirrorC")}),-1.0]])]});
            var Q6;
            Q6=makeQuery(id+"F32.imprint","IMPRINT",FACE,{"disambiguationData":[TD([[makeQuery(id+"F32.imprint","IMPRINT",EDGE,{"derivedFrom":sQuery(id+"F32.wireOp",EDGE,"E139.MirrorC")}),-1.0]])]});
            var Q7;
            Q7=makeQuery(id+"F32.imprint","IMPRINT",FACE,{"disambiguationData":[TD([[makeQuery(id+"F32.imprint","IMPRINT",EDGE,{"derivedFrom":sQuery(id+"F32.wireOp",EDGE,"E143.MirrorC")}),-1.0]])]});
            var Q8;
            Q8=makeQuery(id+"F32.imprint","IMPRINT",FACE,{"disambiguationData":[TD([[makeQuery(id+"F32.imprint","IMPRINT",EDGE,{"derivedFrom":sQuery(id+"F32.wireOp",EDGE,"E142.MirrorC")}),-1.0]])]});
            var Q9;
            Q9=makeQuery(id+"F32.imprint","IMPRINT",FACE,{"disambiguationData":[TD([[makeQuery(id+"F32.imprint","IMPRINT",EDGE,{"derivedFrom":sQuery(id+"F32.wireOp",EDGE,"E146.bottom")}),-1.0]])]});
            var Q10;
            Q10=makeQuery(id+"F32.imprint","IMPRINT",FACE,{"disambiguationData":[TD([[makeQuery(id+"F32.imprint","IMPRINT",EDGE,{"derivedFrom":sQuery(id+"F32.wireOp",EDGE,"E147")}),1.0]])]});
            var Q11;
            Q11=makeQuery(id+"F32.imprint","IMPRINT",FACE,{"disambiguationData":[TD([[makeQuery(id+"F32.imprint","IMPRINT",EDGE,{"derivedFrom":sQuery(id+"F32.wireOp",EDGE,"E148")}),1.0]])]});
            extrude(context, id + "F33", {"entities" : qUnion([Q0, Q1, Q2, Q3, Q4, Q5, Q6, Q7, Q8, Q9, Q10, Q11]), "operationType" : NewBodyOperationType.REMOVE, "oppositeDirection" : true, "depth" : 25 * mm, "offsetDistance" : 25 * mm});
        }
        {
            var Q0;
            Q0=qCreatedBy(makeId("Front.planeOp"),FACE);
            var sketch = newSketch(context, id + "F34", { "sketchPlane" : qUnion([Q0])});
            skCircle(sketch, "E149", {"center": v(0, 0) * mm, "radius": 2.5 * mm});
            skCircle(sketch, "E150", {"center": v(0, 0) * mm, "radius": 13 * mm});
            skSolve(sketch);
        }
        {
            var Q0;
            Q0 = qSketchRegion(id + "F34", true);
            extrude(context, id + "F35", {"entities" : qUnion([Q0]), "depth" : 4.5 * mm, "offsetDistance" : 25 * mm});
        }
        {
            var Q0;
            Q0=makeQuery(id+"F35.opExtrude","CAP_EDGE",EDGE,{"disambiguationData":[OSD([sQuery(id+"F34.wireOp",EDGE,"E149")])],"isStart":false});
            var Q1;
            Q1=makeQuery(id+"F35.opExtrude","CAP_EDGE",EDGE,{"disambiguationData":[OSD([sQuery(id+"F34.wireOp",EDGE,"E150")])],"isStart":false});
            var Q2;
            Q2=makeQuery(id+"F35.opExtrude","CAP_EDGE",EDGE,{"disambiguationData":[OSD([sQuery(id+"F34.wireOp",EDGE,"E150")])],"isStart":true});
            var Q3;
            Q3=makeQuery(id+"F35.opExtrude","CAP_EDGE",EDGE,{"disambiguationData":[OSD([sQuery(id+"F34.wireOp",EDGE,"E149")])],"isStart":true});
            fillet(context, id + "F36", {"entities" : qUnion([Q0, Q1, Q2, Q3]), "radius" : 0.75 * mm, "tangentPropagation" : true, "allowEdgeOverflow" : false});
        }
        {
            var Q0;
            Q0=qCreatedBy(makeId("Front.planeOp"),FACE);
            var sketch = newSketch(context, id + "F37", { "sketchPlane" : qUnion([Q0])});
            skCircle(sketch, "E151", {"center": v(-165.77, -199.59) * mm, "radius": 1.45 * mm});
            skCircle(sketch, "E152", {"center": v(-165.77, -199.59) * mm, "radius": 4 * mm});
            skCircle(sketch, "E153", {"center": v(-129.85, -232.44) * mm, "radius": 1.45 * mm});
            skCircle(sketch, "E154", {"center": v(-129.85, -232.44) * mm, "radius": 4 * mm});
            skSolve(sketch);
        }
        {
            var Q0;
            Q0=makeQuery(id+"F37.imprint","IMPRINT",FACE,{"disambiguationData":[TD([[makeQuery(id+"F37.imprint","IMPRINT",EDGE,{"derivedFrom":sQuery(id+"F37.wireOp",EDGE,"E151")}),-1.0]])]});
            extrude(context, id + "F38", {"entities" : qUnion([Q0]), "depth" : 50 * mm, "offsetDistance" : 25 * mm});
        }
        {
            var Q0;
            Q0=makeQuery(id+"F37.imprint","IMPRINT",FACE,{"disambiguationData":[TD([[makeQuery(id+"F37.imprint","IMPRINT",EDGE,{"derivedFrom":sQuery(id+"F37.wireOp",EDGE,"E153")}),-1.0]])]});
            extrude(context, id + "F39", {"entities" : qUnion([Q0]), "depth" : 35 * mm, "offsetDistance" : 25 * mm});
        }
        {
            var Q0;
            Q0=qCreatedBy(makeId("Front.planeOp"),FACE);
            var sketch = newSketch(context, id + "F40", { "sketchPlane" : qUnion([Q0])});
            skCircle(sketch, "E155", {"center": v(156.05, 199.45) * mm, "radius": 4 * mm});
            skCircle(sketch, "E156", {"center": v(156.05, 199.45) * mm, "radius": 1.45 * mm});
            skSolve(sketch);
        }
        {
            var Q0;
            Q0 = qSketchRegion(id + "F40", true);
            extrude(context, id + "F41", {"entities" : qUnion([Q0]), "depth" : 36 * mm, "offsetDistance" : 25 * mm});
        }
        {
            var Q0;
            Q0=qCreatedBy(makeId("Front.planeOp"),FACE);
            var sketch = newSketch(context, id + "F42", { "sketchPlane" : qUnion([Q0])});
            skCircle(sketch, "E157", {"center": v(129.78, 131.24) * mm, "radius": 1.5 * mm});
            skCircle(sketch, "E158", {"center": v(129.78, 131.24) * mm, "radius": 4 * mm});
            skSolve(sketch);
        }
        {
            var Q0;
            Q0=makeQuery(id+"F42.imprint","IMPRINT",FACE,{"disambiguationData":[TD([[makeQuery(id+"F42.imprint","IMPRINT",EDGE,{"derivedFrom":sQuery(id+"F42.wireOp",EDGE,"E157")}),-1.0]])]});
            extrude(context, id + "F43", {"entities" : qUnion([Q0]), "depth" : 40 * mm, "offsetDistance" : 25 * mm});
        }
        {
            var Q0;
            Q0=qCreatedBy(makeId("Front.planeOp"),FACE);
            var sketch = newSketch(context, id + "F44", { "sketchPlane" : qUnion([Q0])});
            skCircle(sketch, "E159", {"center": v(-237.35, -58.6) * mm, "radius": 10 * mm});
            skCircle(sketch, "E160", {"center": v(-237.35, -58.6) * mm, "radius": 2.75 * mm});
            skSolve(sketch);
        }
        {
            var Q0;
            Q0 = qSketchRegion(id + "F44", true);
            extrude(context, id + "F45", {"entities" : qUnion([Q0]), "depth" : 0.5 * mm, "offsetDistance" : 25 * mm});
        }
        {
            var Q0;
            Q0=qCreatedBy(makeId("Front.planeOp"),FACE);
            var sketch = newSketch(context, id + "F46", { "sketchPlane" : qUnion([Q0])});
            skCircle(sketch, "E161", {"center": v(135.47, 68.14) * mm, "radius": 1.5 * mm});
            skCircle(sketch, "E162", {"center": v(135.47, 68.14) * mm, "radius": 3.5 * mm});
            skSolve(sketch);
        }
        {
            var Q0;
            Q0 = qSketchRegion(id + "F46", true);
            extrude(context, id + "F47", {"entities" : qUnion([Q0]), "depth" : 0.5 * mm, "offsetDistance" : 25 * mm});
        }
        {
            var Q0;
            Q0=qCreatedBy(makeId("Front.planeOp"),FACE);
            var sketch = newSketch(context, id + "F48", { "sketchPlane" : qUnion([Q0])});
            skCircle(sketch, "E163", {"center": v(0, 0) * mm, "radius": 2.45 * mm});
            skSolve(sketch);
        }
        {
            var Q0;
            Q0 = qSketchRegion(id + "F48", true);
            extrude(context, id + "F49", {"entities" : qUnion([Q0]), "depth" : 78 * mm, "offsetDistance" : 25 * mm});
        }
        {
            var Q0;
            Q0=qCreatedBy(makeId("Top.planeOp"),FACE);
            var sketch = newSketch(context, id + "F50", { "sketchPlane" : qUnion([Q0])});
            skLineSegment(sketch, "E164", {"start": v(-14.34, -39) * mm, "end": v(12, -39) * mm, "construction": true});
            skLineSegment(sketch, "E165", {"start": v(11.55, -19) * mm, "end": v(-14.03, -19) * mm, "construction": true});
            skLineSegment(sketch, "E166", {"start": v(12.26, -59) * mm, "end": v(-15.02, -59) * mm, "construction": true});
            skPoint(sketch, "E167", {"position": v(0, -19) * mm});
            skPoint(sketch, "E168", {"position": v(0, -59) * mm});
            skSolve(sketch);
        }
        {
            var Q0;
            Q0=sQuery(id+"F50.wireOp",VERTEX,"E167");
            var Q1;
            Q1=sQuery(id+"F50.wireOp",VERTEX,"E168");
            var Q2;
            Q2=makeQuery(id+"F49.opExtrude","SWEPT_BODY",BODY,{"disambiguationData":[OSD([sQuery(id+"F48.wireOp",EDGE,"E163")])]});
            hole(context, id + "F51", {"style" : HoleStyle.SIMPLE, "endStyle" : HoleEndStyle.THROUGH, "oppositeDirection" : true, "holeDiameter" : 2.5 * mm, "majorDiameter" : 5 * mm, "isTappedThrough" : true, "tappedDepth" : 12 * mm, "tapClearance" : 3, "locations" : qUnion([Q0, Q1]), "scope" : qUnion([Q2])});
        }
        {
            var Q0;
            Q0=qCreatedBy(makeId("Front.planeOp"),FACE);
            var sketch = newSketch(context, id + "F52", { "sketchPlane" : qUnion([Q0])});
            skArc(sketch, "E169", {"start": v(1.25, 2.1) * mm, "mid": v(-2.45, 0) * mm, "end": v(1.25, -2.1) * mm});
            skLineSegment(sketch, "E170", {"start": v(1.25, 2.1) * mm, "end": v(1.25, -2.1) * mm});
            skSolve(sketch);
        }
        {
            var Q0;
            Q0=makeQuery(id+"F52.imprint","IMPRINT",FACE,{"disambiguationData":[TD([[makeQuery(id+"F52.imprint","IMPRINT",EDGE,{"derivedFrom":sQuery(id+"F52.wireOp",EDGE,"E169")}),1.0]])]});
            extrude(context, id + "F53", {"entities" : qUnion([Q0]), "depth" : 78 * mm, "offsetDistance" : 25 * mm});
        }
    });
